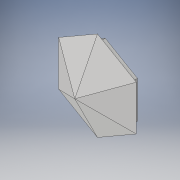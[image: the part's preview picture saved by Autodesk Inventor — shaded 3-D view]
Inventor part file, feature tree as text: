
AUTODESK INVENTOR PART (.ipt)
format: ipt  version: 2019 (Build 230136000, 136)  size: 146,432 bytes
history: native  units: mm
features: sketch x3, extrude x2, plane x1, loft x1, shell x1, other x1
ambient origin geometry x8: Origin, YZ Plane, XZ Plane, XY Plane, X Axis, Y Axis, Z Axis, Center Point
bodies: Solid1 (feature_tree)
feature tree (9):
  sketch  "Sketch1"  dims[d0=200.0mm d1=190.0mm]
  plane  "Work Plane1"
  sketch  "Sketch2"  dims[d2=58.5mm d3=10.0mm d4=0.0mm d5=0.0mm d6=90.0deg]
  extrude  "Extrusion1"  Depth=190.0mm
  loft  "Loft1"
  shell  "Shell1"  Thickness=0.0mm
  extrude  "Extrusion3"  Depth=10.0mm
  other  "Edges1"
  sketch  "Sketch4"  dims[d7=0.0mm d8=90.0deg d17=10.0mm d18=166.0mm d19=20.0mm d20=0.0mm]
